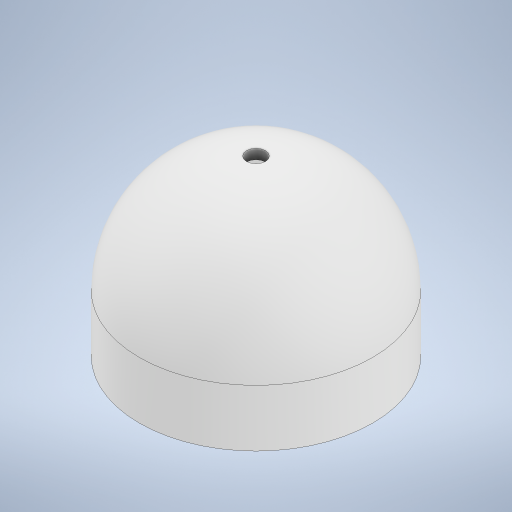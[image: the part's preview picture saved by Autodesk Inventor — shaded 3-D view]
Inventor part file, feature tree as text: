
AUTODESK INVENTOR PART (.ipt)
format: ipt  version: 2023 (Build 270158030, 158C)  size: 262,144 bytes
history: native  units: in
note: dims shown in document units (in); Inventor stores cm internally (conversion verified against a paired STEP export)
features: sketch x2, revolve x1, extrude x1
ambient origin geometry x8: Origin, YZ Plane, XZ Plane, XY Plane, X Axis, Y Axis, Z Axis, Center Point
bodies: Solid1 (feature_tree)
feature tree (4):
  revolve  "Revolution1"  [1 undecoded]
  extrude  "Extrusion1"  Depth=2.816in
  sketch  "Sketch1"  dims[d1=1.5in d2=0.258in]
  sketch  "Sketch2"  dims[d3=90.0deg d4=2.816in d5=0.5in d6=0.0in d7=0.0in]
note: 1 required parameter value undecoded (feature->parameter linkage not recoverable at this tier; creation-order binding heuristic only, values carry confidence <= 0.55)
